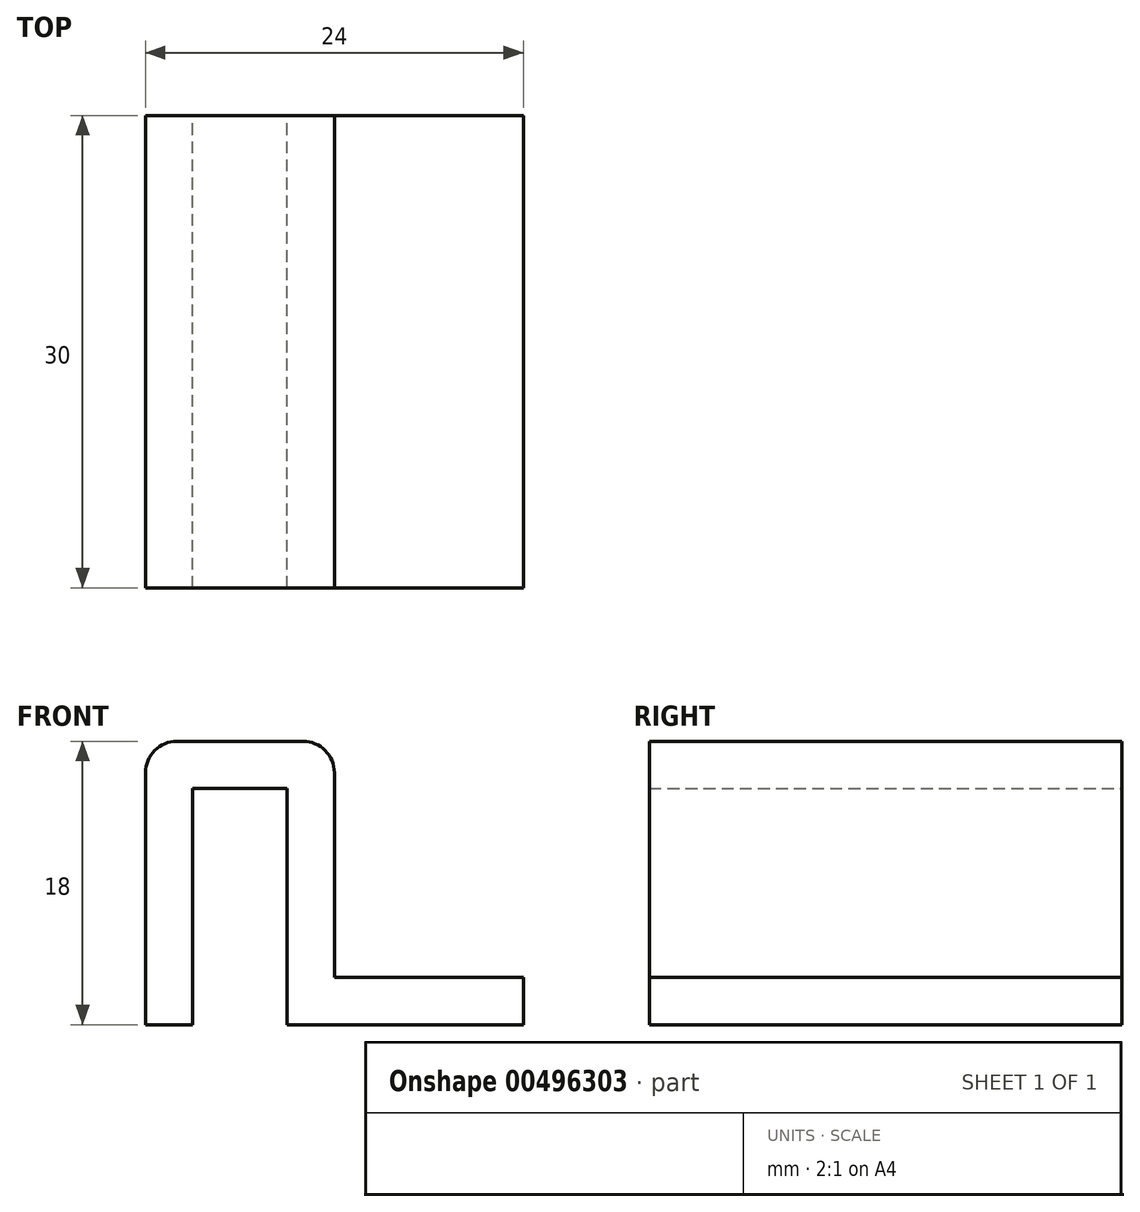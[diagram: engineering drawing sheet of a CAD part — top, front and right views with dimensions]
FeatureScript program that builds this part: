
annotation { "Feature Type Name" : "Feature", "Feature Type Description" : "" }
export const myFeature = defineFeature(function(context is Context, id is Id, definition is map)
    precondition{}
    {
        {
            var Q0;
            Q0=qCreatedBy(makeId("Front.planeOp"),FACE);
            var sketch = newSketch(context, id + "F0", { "sketchPlane" : qUnion([Q0])});
            skLineSegment(sketch, "E0", {"start": v(-6, 15) * mm, "end": v(-6, 0) * mm});
            skLineSegment(sketch, "E1", {"start": v(-6, 15) * mm, "end": v(0, 15) * mm});
            skLineSegment(sketch, "E2", {"start": v(0, 15) * mm, "end": v(0, 0) * mm});
            skLineSegment(sketch, "E3", {"start": v(0, 0) * mm, "end": v(15, 0) * mm});
            skLineSegment(sketch, "E4.0", {"start": v(3, 3) * mm, "end": v(15, 3) * mm});
            skLineSegment(sketch, "E4.1", {"start": v(3, 18) * mm, "end": v(3, 3) * mm});
            skLineSegment(sketch, "E4.2", {"start": v(-9, 18) * mm, "end": v(3, 18) * mm});
            skLineSegment(sketch, "E4.3", {"start": v(-9, 18) * mm, "end": v(-9, 0) * mm});
            skLineSegment(sketch, "E5", {"start": v(-9, 0) * mm, "end": v(-6, 0) * mm});
            skLineSegment(sketch, "E6", {"start": v(15, 3) * mm, "end": v(15, 0) * mm});
            skSolve(sketch);
        }
        {
            var Q0;
            Q0 = qSketchRegion(id + "F0", true);
            extrude(context, id + "F1", {"entities" : qUnion([Q0]), "depth" : 30 * mm});
        }
        {
            var Q0;
            Q0=makeQuery(id+"F1.opExtrude","SWEPT_EDGE",EDGE,{"disambiguationData":[OSD([sQuery(id+"F0.wireOp",EDGE,"E4.1"),sQuery(id+"F0.wireOp",EDGE,"E4.2")])]});
            fillet(context, id + "F2", {"entities" : qUnion([Q0]), "radius" : 2 * mm, "tangentPropagation" : true, "allowEdgeOverflow" : false});
        }
        {
            var Q0;
            Q0=makeQuery(id+"F1.opExtrude","SWEPT_EDGE",EDGE,{"disambiguationData":[OSD([sQuery(id+"F0.wireOp",EDGE,"E4.2"),sQuery(id+"F0.wireOp",EDGE,"E4.3")])]});
            fillet(context, id + "F3", {"entities" : qUnion([Q0]), "radius" : 2 * mm, "tangentPropagation" : true, "allowEdgeOverflow" : false});
        }
    });
